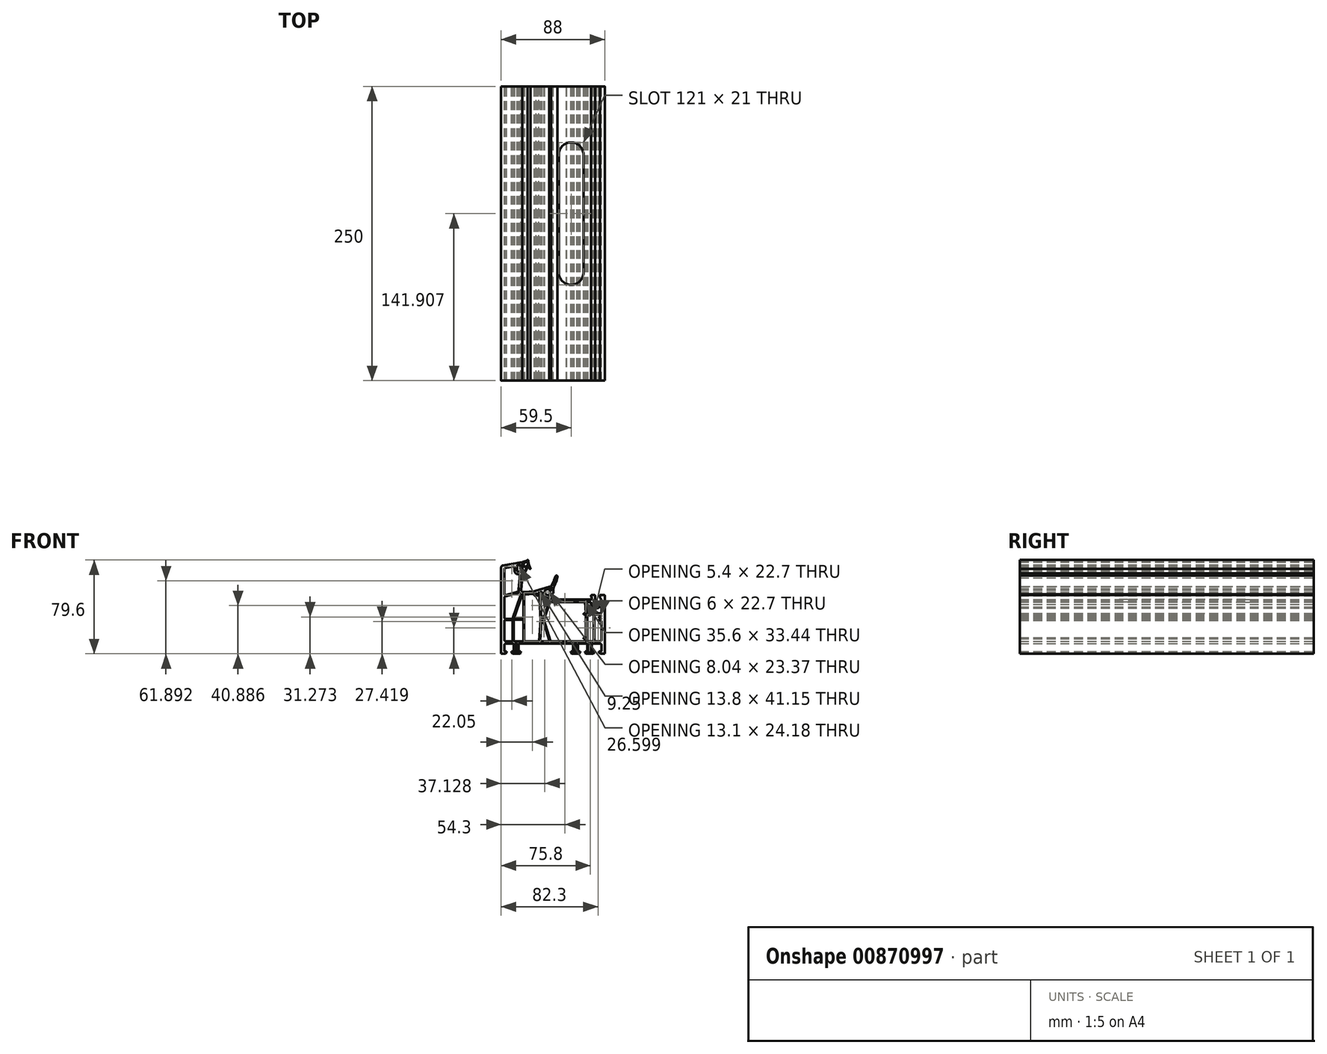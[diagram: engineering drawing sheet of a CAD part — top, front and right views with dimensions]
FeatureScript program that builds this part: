
annotation { "Feature Type Name" : "Feature", "Feature Type Description" : "" }
export const myFeature = defineFeature(function(context is Context, id is Id, definition is map)
    precondition{}
    {
        {
            var Q0;
            Q0=qCreatedBy(makeId("Front.planeOp"),FACE);
            var sketch = newSketch(context, id + "F0", { "sketchPlane" : qUnion([Q0])});
            skLineSegment(sketch, "E0", {"start": v(-41.3, 11) * mm, "end": v(-41.3, 32.34) * mm});
            skArc(sketch, "E1", {"start": v(-40.8, 32.84) * mm, "mid": v(-41.15, 32.7) * mm, "end": v(-41.3, 32.34) * mm});
            skLineSegment(sketch, "E2", {"start": v(-40.8, 32.84) * mm, "end": v(-33.29, 34.17) * mm});
            skArc(sketch, "E3", {"start": v(-32.7, 33.68) * mm, "mid": v(-32.88, 34.06) * mm, "end": v(-33.29, 34.17) * mm});
            skLineSegment(sketch, "E4", {"start": v(-32.7, 33.68) * mm, "end": v(-32.7, 30.97) * mm});
            skArc(sketch, "E5", {"start": v(-32.7, 30.97) * mm, "mid": v(-31.95, 28.92) * mm, "end": v(-30.06, 27.82) * mm});
            skLineSegment(sketch, "E6", {"start": v(-30.06, 27.82) * mm, "end": v(-28.61, 27.57) * mm});
            skArc(sketch, "E7", {"start": v(-28.2, 27.07) * mm, "mid": v(-28.32, 27.4) * mm, "end": v(-28.61, 27.57) * mm});
            skLineSegment(sketch, "E8", {"start": v(-28.2, 27.07) * mm, "end": v(-28.2, 24.7) * mm});
            skLineSegment(sketch, "E9", {"start": v(-28.2, 24.7) * mm, "end": v(-29.18, 14.92) * mm});
            skArc(sketch, "E10", {"start": v(-29.18, 14.92) * mm, "mid": v(-29.19, 14.2) * mm, "end": v(-29.08, 13.48) * mm});
            skArc(sketch, "E11", {"start": v(-29.43, 12.88) * mm, "mid": v(-29.13, 13.1) * mm, "end": v(-29.08, 13.48) * mm});
            skLineSegment(sketch, "E12", {"start": v(-29.43, 12.88) * mm, "end": v(-40.04, 10.04) * mm});
            skArc(sketch, "E13", {"start": v(-41.3, 11) * mm, "mid": v(-40.9, 10.2) * mm, "end": v(-40.04, 10.04) * mm});
            skLineSegment(sketch, "E14", {"start": v(-41.3, -9.1) * mm, "end": v(-41.3, 7.8) * mm});
            skArc(sketch, "E15", {"start": v(-40.56, 8.76) * mm, "mid": v(-41.1, 8.4) * mm, "end": v(-41.3, 7.8) * mm});
            skLineSegment(sketch, "E16", {"start": v(-40.56, 8.76) * mm, "end": v(-28.7, 11.94) * mm});
            skArc(sketch, "E17", {"start": v(-28.2, 11.78) * mm, "mid": v(-28.43, 11.93) * mm, "end": v(-28.7, 11.94) * mm});
            skArc(sketch, "E18", {"start": v(-28.2, 11.78) * mm, "mid": v(-27.87, 11.43) * mm, "end": v(-27.5, 11.13) * mm});
            skArc(sketch, "E19", {"start": v(-27.33, 10.56) * mm, "mid": v(-27.32, 10.87) * mm, "end": v(-27.5, 11.13) * mm});
            skLineSegment(sketch, "E20", {"start": v(-27.33, 10.56) * mm, "end": v(-34.25, -9.76) * mm});
            skArc(sketch, "E21", {"start": v(-34.72, -10.1) * mm, "mid": v(-34.43, -10) * mm, "end": v(-34.25, -9.76) * mm});
            skLineSegment(sketch, "E22", {"start": v(-34.72, -10.1) * mm, "end": v(-40.3, -10.1) * mm});
            skArc(sketch, "E23", {"start": v(-41.3, -9.1) * mm, "mid": v(-41, -9.8) * mm, "end": v(-40.3, -10.1) * mm});
            skLineSegment(sketch, "E24", {"start": v(-41.3, -28.1) * mm, "end": v(-41.3, -12.2) * mm});
            skArc(sketch, "E25", {"start": v(-40.3, -11.2) * mm, "mid": v(-41, -11.5) * mm, "end": v(-41.3, -12.2) * mm});
            skLineSegment(sketch, "E26", {"start": v(-40.3, -11.2) * mm, "end": v(-34.8, -11.2) * mm});
            skArc(sketch, "E27", {"start": v(-34.3, -11.7) * mm, "mid": v(-34.45, -11.35) * mm, "end": v(-34.8, -11.2) * mm});
            skLineSegment(sketch, "E28", {"start": v(-34.3, -11.7) * mm, "end": v(-34.3, -28.6) * mm});
            skArc(sketch, "E29", {"start": v(-34.8, -29.1) * mm, "mid": v(-34.45, -28.95) * mm, "end": v(-34.3, -28.6) * mm});
            skLineSegment(sketch, "E30", {"start": v(-34.8, -29.1) * mm, "end": v(-40.3, -29.1) * mm});
            skArc(sketch, "E31", {"start": v(-41.3, -28.1) * mm, "mid": v(-41, -28.8) * mm, "end": v(-40.3, -29.1) * mm});
            skLineSegment(sketch, "E32", {"start": v(-33.2, -28.6) * mm, "end": v(-33.2, -11.4) * mm});
            skArc(sketch, "E33", {"start": v(-32.7, -10.9) * mm, "mid": v(-33.05, -11.05) * mm, "end": v(-33.2, -11.4) * mm});
            skLineSegment(sketch, "E34", {"start": v(-32.7, -10.9) * mm, "end": v(-25.6, -10.9) * mm});
            skArc(sketch, "E35", {"start": v(-25.1, -11.4) * mm, "mid": v(-25.25, -11.05) * mm, "end": v(-25.6, -10.9) * mm});
            skLineSegment(sketch, "E36", {"start": v(-25.1, -11.4) * mm, "end": v(-25.1, -28.6) * mm});
            skArc(sketch, "E37", {"start": v(-25.6, -29.1) * mm, "mid": v(-25.25, -28.95) * mm, "end": v(-25.1, -28.6) * mm});
            skLineSegment(sketch, "E38", {"start": v(-25.6, -29.1) * mm, "end": v(-32.7, -29.1) * mm});
            skArc(sketch, "E39", {"start": v(-33.2, -28.6) * mm, "mid": v(-33.05, -28.95) * mm, "end": v(-32.7, -29.1) * mm});
            skLineSegment(sketch, "E40", {"start": v(-32.4, -31.8) * mm, "end": v(-32.4, -37.3) * mm});
            skArc(sketch, "E41", {"start": v(-32.84, -38.28) * mm, "mid": v(-32.52, -37.83) * mm, "end": v(-32.4, -37.3) * mm});
            skArc(sketch, "E42", {"start": v(-32.84, -38.27) * mm, "mid": v(-32.92, -38.6) * mm, "end": v(-32.64, -38.8) * mm});
            skLineSegment(sketch, "E43", {"start": v(-32.64, -38.8) * mm, "end": v(-29.76, -38.8) * mm});
            skArc(sketch, "E44", {"start": v(-29.76, -38.8) * mm, "mid": v(-29.48, -38.6) * mm, "end": v(-29.56, -38.27) * mm});
            skArc(sketch, "E45", {"start": v(-30, -37.3) * mm, "mid": v(-29.88, -37.83) * mm, "end": v(-29.56, -38.28) * mm});
            skLineSegment(sketch, "E46", {"start": v(-30, -37.3) * mm, "end": v(-30, -31.8) * mm});
            skArc(sketch, "E47", {"start": v(-30, -31.8) * mm, "mid": v(-30.15, -31.45) * mm, "end": v(-30.5, -31.3) * mm});
            skLineSegment(sketch, "E48", {"start": v(-30.5, -31.3) * mm, "end": v(-31.9, -31.3) * mm});
            skArc(sketch, "E49", {"start": v(-31.9, -31.3) * mm, "mid": v(-32.25, -31.45) * mm, "end": v(-32.4, -31.8) * mm});
            skLineSegment(sketch, "E50", {"start": v(-32.97, -9.44) * mm, "end": v(-26.34, 10.04) * mm});
            skArc(sketch, "E51", {"start": v(-25.78, 10.37) * mm, "mid": v(-26.12, 10.31) * mm, "end": v(-26.34, 10.04) * mm});
            skLineSegment(sketch, "E52", {"start": v(-25.78, 10.37) * mm, "end": v(-25.54, 10.33) * mm});
            skArc(sketch, "E53", {"start": v(-25.1, 9.84) * mm, "mid": v(-25.23, 10.17) * mm, "end": v(-25.54, 10.33) * mm});
            skLineSegment(sketch, "E54", {"start": v(-25.1, 9.84) * mm, "end": v(-25.1, -9.6) * mm});
            skArc(sketch, "E55", {"start": v(-25.6, -10.1) * mm, "mid": v(-25.25, -9.95) * mm, "end": v(-25.1, -9.6) * mm});
            skLineSegment(sketch, "E56", {"start": v(-25.6, -10.1) * mm, "end": v(-32.5, -10.1) * mm});
            skArc(sketch, "E57", {"start": v(-32.97, -9.44) * mm, "mid": v(-32.9, -9.9) * mm, "end": v(-32.5, -10.1) * mm});
            skLineSegment(sketch, "E58", {"start": v(-24.3, -28.6) * mm, "end": v(-24.3, 9.89) * mm});
            skArc(sketch, "E59", {"start": v(-23.84, 10.39) * mm, "mid": v(-24.17, 10.22) * mm, "end": v(-24.3, 9.89) * mm});
            skLineSegment(sketch, "E60", {"start": v(-23.84, 10.39) * mm, "end": v(-16.44, 11.03) * mm});
            skArc(sketch, "E61", {"start": v(-15.9, 10.53) * mm, "mid": v(-16.06, 10.9) * mm, "end": v(-16.44, 11.03) * mm});
            skLineSegment(sketch, "E62", {"start": v(-15.9, 10.53) * mm, "end": v(-15.9, 10.16) * mm});
            skArc(sketch, "E63", {"start": v(-15.9, 10.16) * mm, "mid": v(-15.3, 9.56) * mm, "end": v(-14.7, 10.16) * mm});
            skLineSegment(sketch, "E64", {"start": v(-14.7, 10.16) * mm, "end": v(-14.7, 10.9) * mm});
            skArc(sketch, "E65", {"start": v(-13.7, 10.9) * mm, "mid": v(-14.2, 11.4) * mm, "end": v(-14.7, 10.9) * mm});
            skLineSegment(sketch, "E66", {"start": v(-13.7, 10.9) * mm, "end": v(-13.7, 10.16) * mm});
            skArc(sketch, "E67", {"start": v(-13.7, 10.16) * mm, "mid": v(-13.1, 9.56) * mm, "end": v(-12.5, 10.16) * mm});
            skLineSegment(sketch, "E68", {"start": v(-12.5, 10.16) * mm, "end": v(-12.5, 11.63) * mm});
            skArc(sketch, "E69", {"start": v(-11.67, 11.65) * mm, "mid": v(-12.1, 12.05) * mm, "end": v(-12.5, 11.63) * mm});
            skLineSegment(sketch, "E70", {"start": v(-11.67, 11.65) * mm, "end": v(-10.5, -11.03) * mm});
            skLineSegment(sketch, "E71", {"start": v(-10.5, -11.03) * mm, "end": v(-11.67, -28.63) * mm});
            skArc(sketch, "E72", {"start": v(-12.17, -29.1) * mm, "mid": v(-11.83, -28.97) * mm, "end": v(-11.67, -28.63) * mm});
            skLineSegment(sketch, "E73", {"start": v(-12.17, -29.1) * mm, "end": v(-23.8, -29.1) * mm});
            skArc(sketch, "E74", {"start": v(-24.3, -28.6) * mm, "mid": v(-24.15, -28.95) * mm, "end": v(-23.8, -29.1) * mm});
            skLineSegment(sketch, "E75", {"start": v(-10.9, 12.03) * mm, "end": v(-9.74, -10.13) * mm});
            skArc(sketch, "E76", {"start": v(-9.74, -10.13) * mm, "mid": v(-9.59, -10.46) * mm, "end": v(-9.24, -10.6) * mm});
            skLineSegment(sketch, "E77", {"start": v(-9.24, -10.6) * mm, "end": v(-8.6, -10.6) * mm});
            skArc(sketch, "E78", {"start": v(-8.6, -10.6) * mm, "mid": v(-8.3, -10.5) * mm, "end": v(-8.12, -10.26) * mm});
            skLineSegment(sketch, "E79", {"start": v(-8.12, -10.26) * mm, "end": v(-2.88, 5.09) * mm});
            skArc(sketch, "E80", {"start": v(-2.88, 5.09) * mm, "mid": v(-2.85, 5.25) * mm, "end": v(-2.88, 5.41) * mm});
            skArc(sketch, "E81", {"start": v(-3.2, 6.76) * mm, "mid": v(-3.14, 6.13) * mm, "end": v(-2.94, 5.53) * mm});
            skArc(sketch, "E82", {"start": v(-3.2, 6.76) * mm, "mid": v(-3.28, 7.05) * mm, "end": v(-3.51, 7.24) * mm});
            skLineSegment(sketch, "E83", {"start": v(-3.51, 7.24) * mm, "end": v(-6.89, 8.6) * mm});
            skArc(sketch, "E84", {"start": v(-8.63, 10.05) * mm, "mid": v(-7.87, 9.2) * mm, "end": v(-6.89, 8.6) * mm});
            skArc(sketch, "E85", {"start": v(-9.2, 12.24) * mm, "mid": v(-9.08, 11.1) * mm, "end": v(-8.63, 10.05) * mm});
            skArc(sketch, "E86", {"start": v(-9.2, 12.24) * mm, "mid": v(-9.38, 12.67) * mm, "end": v(-9.84, 12.75) * mm});
            skLineSegment(sketch, "E87", {"start": v(-9.84, 12.75) * mm, "end": v(-10.54, 12.54) * mm});
            skArc(sketch, "E88", {"start": v(-10.54, 12.54) * mm, "mid": v(-10.8, 12.35) * mm, "end": v(-10.9, 12.03) * mm});
            skLineSegment(sketch, "E89", {"start": v(-10.86, -28.57) * mm, "end": v(-9.75, -11.87) * mm});
            skArc(sketch, "E90", {"start": v(-9.26, -11.4) * mm, "mid": v(-9.6, -11.53) * mm, "end": v(-9.75, -11.87) * mm});
            skLineSegment(sketch, "E91", {"start": v(-9.26, -11.4) * mm, "end": v(-8.61, -11.4) * mm});
            skArc(sketch, "E92", {"start": v(-8.13, -11.76) * mm, "mid": v(-8.31, -11.5) * mm, "end": v(-8.61, -11.4) * mm});
            skLineSegment(sketch, "E93", {"start": v(-8.13, -11.76) * mm, "end": v(-3.13, -28.46) * mm});
            skArc(sketch, "E94", {"start": v(-3.6, -29.1) * mm, "mid": v(-3.2, -28.9) * mm, "end": v(-3.13, -28.46) * mm});
            skLineSegment(sketch, "E95", {"start": v(-3.6, -29.1) * mm, "end": v(-10.36, -29.1) * mm});
            skArc(sketch, "E96", {"start": v(-10.86, -28.57) * mm, "mid": v(-10.73, -28.94) * mm, "end": v(-10.36, -29.1) * mm});
            skArc(sketch, "E97", {"start": v(-10.86, -28.57) * mm, "mid": v(-10.86, -28.57) * mm, "end": v(-10.86, -28.57) * mm});
            skLineSegment(sketch, "E98", {"start": v(-0.5, 4) * mm, "end": v(26.99, 4) * mm});
            skArc(sketch, "E99", {"start": v(27.28, 3.73) * mm, "mid": v(27.19, 3.92) * mm, "end": v(26.99, 4) * mm});
            skLineSegment(sketch, "E100", {"start": v(27.28, 3.73) * mm, "end": v(28.05, -5.06) * mm});
            skArc(sketch, "E101", {"start": v(27.55, -5.6) * mm, "mid": v(27.92, -5.44) * mm, "end": v(28.05, -5.06) * mm});
            skLineSegment(sketch, "E102", {"start": v(27.55, -5.6) * mm, "end": v(26.4, -5.6) * mm});
            skArc(sketch, "E103", {"start": v(26.4, -5.6) * mm, "mid": v(26.19, -5.69) * mm, "end": v(26.1, -5.9) * mm});
            skLineSegment(sketch, "E104", {"start": v(26.1, -5.9) * mm, "end": v(26.1, -6.1) * mm});
            skArc(sketch, "E105", {"start": v(26.1, -6.1) * mm, "mid": v(26.19, -6.31) * mm, "end": v(26.4, -6.4) * mm});
            skLineSegment(sketch, "E106", {"start": v(26.4, -6.4) * mm, "end": v(27.6, -6.4) * mm});
            skArc(sketch, "E107", {"start": v(28.1, -6.9) * mm, "mid": v(27.95, -6.55) * mm, "end": v(27.6, -6.4) * mm});
            skLineSegment(sketch, "E108", {"start": v(28.1, -6.9) * mm, "end": v(28.1, -25.7) * mm});
            skArc(sketch, "E109", {"start": v(27.6, -26.2) * mm, "mid": v(27.95, -26.05) * mm, "end": v(28.1, -25.7) * mm});
            skLineSegment(sketch, "E110", {"start": v(27.6, -26.2) * mm, "end": v(26.4, -26.2) * mm});
            skArc(sketch, "E111", {"start": v(26.4, -26.2) * mm, "mid": v(26.19, -26.29) * mm, "end": v(26.1, -26.5) * mm});
            skLineSegment(sketch, "E112", {"start": v(26.1, -26.5) * mm, "end": v(26.1, -26.7) * mm});
            skArc(sketch, "E113", {"start": v(26.1, -26.7) * mm, "mid": v(26.19, -26.91) * mm, "end": v(26.4, -27) * mm});
            skLineSegment(sketch, "E114", {"start": v(26.4, -27) * mm, "end": v(27.6, -27) * mm});
            skArc(sketch, "E115", {"start": v(28.1, -27.5) * mm, "mid": v(27.95, -27.15) * mm, "end": v(27.6, -27) * mm});
            skLineSegment(sketch, "E116", {"start": v(28.1, -27.5) * mm, "end": v(28.1, -28.8) * mm});
            skArc(sketch, "E117", {"start": v(27.8, -29.1) * mm, "mid": v(28.01, -29.01) * mm, "end": v(28.1, -28.8) * mm});
            skLineSegment(sketch, "E118", {"start": v(27.8, -29.1) * mm, "end": v(-1.73, -29.1) * mm});
            skArc(sketch, "E119", {"start": v(-2.2, -28.74) * mm, "mid": v(-2.03, -29) * mm, "end": v(-1.73, -29.1) * mm});
            skLineSegment(sketch, "E120", {"start": v(-2.2, -28.74) * mm, "end": v(-7.48, -11.15) * mm});
            skArc(sketch, "E121", {"start": v(-7.48, -10.87) * mm, "mid": v(-7.5, -11) * mm, "end": v(-7.48, -11.15) * mm});
            skLineSegment(sketch, "E122", {"start": v(-7.48, -10.87) * mm, "end": v(-2.4, 4) * mm});
            skArc(sketch, "E123", {"start": v(-1.7, 4.29) * mm, "mid": v(-2.12, 4.3) * mm, "end": v(-2.4, 4) * mm});
            skArc(sketch, "E124", {"start": v(-1.7, 4.29) * mm, "mid": v(-1.42, 4.16) * mm, "end": v(-1.12, 4.07) * mm});
            skArc(sketch, "E125", {"start": v(-1.12, 4.07) * mm, "mid": v(-0.81, 4.02) * mm, "end": v(-0.5, 4) * mm});
            skLineSegment(sketch, "E126", {"start": v(28.31, 3.46) * mm, "end": v(29.06, -5.14) * mm});
            skArc(sketch, "E127", {"start": v(29.06, -5.14) * mm, "mid": v(29.22, -5.47) * mm, "end": v(29.56, -5.6) * mm});
            skLineSegment(sketch, "E128", {"start": v(29.56, -5.6) * mm, "end": v(34, -5.6) * mm});
            skArc(sketch, "E129", {"start": v(34, -5.6) * mm, "mid": v(34.35, -5.45) * mm, "end": v(34.5, -5.1) * mm});
            skLineSegment(sketch, "E130", {"start": v(34.5, -5.1) * mm, "end": v(34.5, -0.18) * mm});
            skArc(sketch, "E131", {"start": v(34.5, -0.18) * mm, "mid": v(34.42, 0.1) * mm, "end": v(34.2, 0.27) * mm});
            skArc(sketch, "E132", {"start": v(32.3, 3.2) * mm, "mid": v(32.82, 1.46) * mm, "end": v(34.2, 0.27) * mm});
            skLineSegment(sketch, "E133", {"start": v(32.3, 3.2) * mm, "end": v(32.3, 3.5) * mm});
            skArc(sketch, "E134", {"start": v(32.3, 3.5) * mm, "mid": v(32.15, 3.85) * mm, "end": v(31.8, 4) * mm});
            skLineSegment(sketch, "E135", {"start": v(31.8, 4) * mm, "end": v(28.8, 4) * mm});
            skArc(sketch, "E136", {"start": v(28.8, 4) * mm, "mid": v(28.44, 3.84) * mm, "end": v(28.31, 3.46) * mm});
            skLineSegment(sketch, "E137", {"start": v(35.3, -5.1) * mm, "end": v(35.3, -0.5) * mm});
            skArc(sketch, "E138", {"start": v(35.8, 0) * mm, "mid": v(35.45, -0.15) * mm, "end": v(35.3, -0.5) * mm});
            skLineSegment(sketch, "E139", {"start": v(35.8, 0) * mm, "end": v(36.6, 0) * mm});
            skArc(sketch, "E140", {"start": v(37.1, -0.5) * mm, "mid": v(36.95, -0.15) * mm, "end": v(36.6, 0) * mm});
            skLineSegment(sketch, "E141", {"start": v(37.1, -0.5) * mm, "end": v(37.1, -0.6) * mm});
            skArc(sketch, "E142", {"start": v(37.1, -0.6) * mm, "mid": v(37.25, -0.95) * mm, "end": v(37.6, -1.1) * mm});
            skLineSegment(sketch, "E143", {"start": v(37.6, -1.1) * mm, "end": v(38.4, -1.1) * mm});
            skArc(sketch, "E144", {"start": v(38.4, -1.1) * mm, "mid": v(38.75, -0.95) * mm, "end": v(38.9, -0.6) * mm});
            skLineSegment(sketch, "E145", {"start": v(38.9, -0.6) * mm, "end": v(38.9, -0.5) * mm});
            skArc(sketch, "E146", {"start": v(39.4, 0) * mm, "mid": v(39.05, -0.15) * mm, "end": v(38.9, -0.5) * mm});
            skLineSegment(sketch, "E147", {"start": v(39.4, 0) * mm, "end": v(40.3, 0) * mm});
            skArc(sketch, "E148", {"start": v(41.3, -1) * mm, "mid": v(41, -0.3) * mm, "end": v(40.3, 0) * mm});
            skLineSegment(sketch, "E149", {"start": v(41.3, -1) * mm, "end": v(41.3, -4.6) * mm});
            skArc(sketch, "E150", {"start": v(40.3, -5.6) * mm, "mid": v(41, -5.3) * mm, "end": v(41.3, -4.6) * mm});
            skLineSegment(sketch, "E151", {"start": v(40.3, -5.6) * mm, "end": v(35.8, -5.6) * mm});
            skArc(sketch, "E152", {"start": v(35.3, -5.1) * mm, "mid": v(35.45, -5.45) * mm, "end": v(35.8, -5.6) * mm});
            skLineSegment(sketch, "E153", {"start": v(29.1, -6.9) * mm, "end": v(29.1, -28.6) * mm});
            skArc(sketch, "E154", {"start": v(29.1, -28.6) * mm, "mid": v(29.25, -28.95) * mm, "end": v(29.6, -29.1) * mm});
            skLineSegment(sketch, "E155", {"start": v(29.6, -29.1) * mm, "end": v(34, -29.1) * mm});
            skArc(sketch, "E156", {"start": v(34, -29.1) * mm, "mid": v(34.35, -28.95) * mm, "end": v(34.5, -28.6) * mm});
            skLineSegment(sketch, "E157", {"start": v(34.5, -28.6) * mm, "end": v(34.5, -6.9) * mm});
            skArc(sketch, "E158", {"start": v(34.5, -6.9) * mm, "mid": v(34.35, -6.55) * mm, "end": v(34, -6.4) * mm});
            skLineSegment(sketch, "E159", {"start": v(34, -6.4) * mm, "end": v(29.6, -6.4) * mm});
            skArc(sketch, "E160", {"start": v(29.6, -6.4) * mm, "mid": v(29.25, -6.55) * mm, "end": v(29.1, -6.9) * mm});
            skLineSegment(sketch, "E161", {"start": v(35.3, -6.9) * mm, "end": v(35.3, -28.6) * mm});
            skArc(sketch, "E162", {"start": v(35.3, -28.6) * mm, "mid": v(35.45, -28.95) * mm, "end": v(35.8, -29.1) * mm});
            skLineSegment(sketch, "E163", {"start": v(35.8, -29.1) * mm, "end": v(40.3, -29.1) * mm});
            skArc(sketch, "E164", {"start": v(40.3, -29.1) * mm, "mid": v(41, -28.8) * mm, "end": v(41.3, -28.1) * mm});
            skLineSegment(sketch, "E165", {"start": v(41.3, -28.1) * mm, "end": v(41.3, -12.6) * mm});
            skArc(sketch, "E166", {"start": v(41.3, -12.6) * mm, "mid": v(41, -11.9) * mm, "end": v(40.3, -11.6) * mm});
            skLineSegment(sketch, "E167", {"start": v(40.3, -11.6) * mm, "end": v(39.6, -11.6) * mm});
            skArc(sketch, "E168", {"start": v(39.6, -10.4) * mm, "mid": v(39, -11) * mm, "end": v(39.6, -11.6) * mm});
            skLineSegment(sketch, "E169", {"start": v(39.6, -10.4) * mm, "end": v(40.5, -10.4) * mm});
            skArc(sketch, "E170", {"start": v(40.5, -10.4) * mm, "mid": v(41, -9.9) * mm, "end": v(40.5, -9.4) * mm});
            skLineSegment(sketch, "E171", {"start": v(40.5, -9.4) * mm, "end": v(39.6, -9.4) * mm});
            skArc(sketch, "E172", {"start": v(39.6, -8.2) * mm, "mid": v(39, -8.8) * mm, "end": v(39.6, -9.4) * mm});
            skLineSegment(sketch, "E173", {"start": v(39.6, -8.2) * mm, "end": v(40.5, -8.2) * mm});
            skArc(sketch, "E174", {"start": v(40.5, -8.2) * mm, "mid": v(41, -7.7) * mm, "end": v(40.5, -7.2) * mm});
            skLineSegment(sketch, "E175", {"start": v(40.5, -7.2) * mm, "end": v(39.6, -7.2) * mm});
            skArc(sketch, "E176", {"start": v(39.02, -6.76) * mm, "mid": v(39.24, -7.08) * mm, "end": v(39.6, -7.2) * mm});
            skArc(sketch, "E177", {"start": v(39.02, -6.76) * mm, "mid": v(38.84, -6.5) * mm, "end": v(38.54, -6.4) * mm});
            skLineSegment(sketch, "E178", {"start": v(38.54, -6.4) * mm, "end": v(35.8, -6.4) * mm});
            skArc(sketch, "E179", {"start": v(35.8, -6.4) * mm, "mid": v(35.45, -6.55) * mm, "end": v(35.3, -6.9) * mm});
            skLineSegment(sketch, "E180", {"start": v(30, -31.8) * mm, "end": v(30, -37.3) * mm});
            skArc(sketch, "E181", {"start": v(29.56, -38.28) * mm, "mid": v(29.88, -37.83) * mm, "end": v(30, -37.3) * mm});
            skArc(sketch, "E182", {"start": v(29.56, -38.27) * mm, "mid": v(29.48, -38.6) * mm, "end": v(29.76, -38.8) * mm});
            skLineSegment(sketch, "E183", {"start": v(29.76, -38.8) * mm, "end": v(32.64, -38.8) * mm});
            skArc(sketch, "E184", {"start": v(32.64, -38.8) * mm, "mid": v(32.92, -38.6) * mm, "end": v(32.84, -38.27) * mm});
            skArc(sketch, "E185", {"start": v(32.4, -37.3) * mm, "mid": v(32.52, -37.83) * mm, "end": v(32.84, -38.28) * mm});
            skLineSegment(sketch, "E186", {"start": v(32.4, -37.3) * mm, "end": v(32.4, -31.8) * mm});
            skArc(sketch, "E187", {"start": v(32.4, -31.8) * mm, "mid": v(32.25, -31.45) * mm, "end": v(31.9, -31.3) * mm});
            skLineSegment(sketch, "E188", {"start": v(31.9, -31.3) * mm, "end": v(30.5, -31.3) * mm});
            skArc(sketch, "E189", {"start": v(30.5, -31.3) * mm, "mid": v(30.15, -31.45) * mm, "end": v(30, -31.8) * mm});
            skLineSegment(sketch, "E190", {"start": v(18, -37.3) * mm, "end": v(18, -31.8) * mm});
            skArc(sketch, "E191", {"start": v(18.5, -31.3) * mm, "mid": v(18.15, -31.45) * mm, "end": v(18, -31.8) * mm});
            skLineSegment(sketch, "E192", {"start": v(18.5, -31.3) * mm, "end": v(19.9, -31.3) * mm});
            skArc(sketch, "E193", {"start": v(20.4, -31.8) * mm, "mid": v(20.25, -31.45) * mm, "end": v(19.9, -31.3) * mm});
            skLineSegment(sketch, "E194", {"start": v(20.4, -31.8) * mm, "end": v(20.4, -37.3) * mm});
            skArc(sketch, "E195", {"start": v(20.4, -37.3) * mm, "mid": v(20.52, -37.83) * mm, "end": v(20.84, -38.27) * mm});
            skArc(sketch, "E196", {"start": v(20.64, -38.8) * mm, "mid": v(20.92, -38.6) * mm, "end": v(20.84, -38.27) * mm});
            skLineSegment(sketch, "E197", {"start": v(20.64, -38.8) * mm, "end": v(17.76, -38.8) * mm});
            skArc(sketch, "E198", {"start": v(17.56, -38.28) * mm, "mid": v(17.48, -38.6) * mm, "end": v(17.76, -38.8) * mm});
            skArc(sketch, "E199", {"start": v(17.56, -38.28) * mm, "mid": v(17.88, -37.83) * mm, "end": v(18, -37.3) * mm});
            skLineSegment(sketch, "E200", {"start": v(30.5, -31.3) * mm, "end": v(31.9, -31.3) * mm});
            skLineSegment(sketch, "E201", {"start": v(32.4, -31.8) * mm, "end": v(32.4, -37.3) * mm});
            skLineSegment(sketch, "E202", {"start": v(32.64, -38.8) * mm, "end": v(29.76, -38.8) * mm});
            skLineSegment(sketch, "E203", {"start": v(30, -37.3) * mm, "end": v(30, -31.8) * mm});
            skArc(sketch, "E204", {"start": v(17.56, -38.28) * mm, "mid": v(17.89, -37.83) * mm, "end": v(18, -37.3) * mm});
            skLineSegment(sketch, "E205", {"start": v(35.8, -6.4) * mm, "end": v(38.54, -6.4) * mm});
            skLineSegment(sketch, "E206", {"start": v(39.6, -7.2) * mm, "end": v(40.5, -7.2) * mm});
            skLineSegment(sketch, "E207", {"start": v(40.5, -8.2) * mm, "end": v(39.6, -8.2) * mm});
            skLineSegment(sketch, "E208", {"start": v(39.6, -9.4) * mm, "end": v(40.5, -9.4) * mm});
            skLineSegment(sketch, "E209", {"start": v(40.5, -10.4) * mm, "end": v(39.6, -10.4) * mm});
            skLineSegment(sketch, "E210", {"start": v(39.6, -11.6) * mm, "end": v(40.3, -11.6) * mm});
            skLineSegment(sketch, "E211", {"start": v(41.3, -12.6) * mm, "end": v(41.3, -28.1) * mm});
            skLineSegment(sketch, "E212", {"start": v(40.3, -29.1) * mm, "end": v(35.8, -29.1) * mm});
            skLineSegment(sketch, "E213", {"start": v(35.3, -28.6) * mm, "end": v(35.3, -6.9) * mm});
            skArc(sketch, "E214", {"start": v(38.4, -1.1) * mm, "mid": v(38.77, -0.94) * mm, "end": v(38.9, -0.55) * mm});
            skArc(sketch, "E215", {"start": v(39.4, 0) * mm, "mid": v(39.03, -0.16) * mm, "end": v(38.9, -0.55) * mm});
            skLineSegment(sketch, "E216", {"start": v(29.6, -6.4) * mm, "end": v(34, -6.4) * mm});
            skLineSegment(sketch, "E217", {"start": v(34.5, -6.9) * mm, "end": v(34.5, -28.6) * mm});
            skLineSegment(sketch, "E218", {"start": v(34, -29.1) * mm, "end": v(29.6, -29.1) * mm});
            skLineSegment(sketch, "E219", {"start": v(29.1, -28.6) * mm, "end": v(29.1, -6.9) * mm});
            skLineSegment(sketch, "E220", {"start": v(28.8, 4) * mm, "end": v(31.8, 4) * mm});
            skLineSegment(sketch, "E221", {"start": v(32.3, 3.5) * mm, "end": v(32.3, 3.2) * mm});
            skLineSegment(sketch, "E222", {"start": v(34.5, -0.18) * mm, "end": v(34.5, -5.1) * mm});
            skLineSegment(sketch, "E223", {"start": v(34, -5.6) * mm, "end": v(29.56, -5.6) * mm});
            skLineSegment(sketch, "E224", {"start": v(29.06, -5.14) * mm, "end": v(28.31, 3.46) * mm});
            skLineSegment(sketch, "E225", {"start": v(-31.9, -31.3) * mm, "end": v(-30.5, -31.3) * mm});
            skLineSegment(sketch, "E226", {"start": v(-30, -31.8) * mm, "end": v(-30, -37.3) * mm});
            skLineSegment(sketch, "E227", {"start": v(-29.76, -38.8) * mm, "end": v(-32.64, -38.8) * mm});
            skLineSegment(sketch, "E228", {"start": v(-32.4, -37.3) * mm, "end": v(-32.4, -31.8) * mm});
            skLineSegment(sketch, "E229", {"start": v(-1.73, -29.1) * mm, "end": v(27.8, -29.1) * mm});
            skLineSegment(sketch, "E230", {"start": v(28.1, -28.8) * mm, "end": v(28.1, -27.5) * mm});
            skLineSegment(sketch, "E231", {"start": v(27.6, -27) * mm, "end": v(26.4, -27) * mm});
            skLineSegment(sketch, "E232", {"start": v(26.1, -26.7) * mm, "end": v(26.1, -26.5) * mm});
            skLineSegment(sketch, "E233", {"start": v(26.4, -26.2) * mm, "end": v(27.6, -26.2) * mm});
            skLineSegment(sketch, "E234", {"start": v(28.1, -25.7) * mm, "end": v(28.1, -6.9) * mm});
            skLineSegment(sketch, "E235", {"start": v(27.6, -6.4) * mm, "end": v(26.4, -6.4) * mm});
            skLineSegment(sketch, "E236", {"start": v(26.1, -6.1) * mm, "end": v(26.1, -5.9) * mm});
            skLineSegment(sketch, "E237", {"start": v(26.4, -5.6) * mm, "end": v(27.55, -5.6) * mm});
            skLineSegment(sketch, "E238", {"start": v(28.05, -5.06) * mm, "end": v(27.28, 3.73) * mm});
            skLineSegment(sketch, "E239", {"start": v(26.99, 4) * mm, "end": v(-0.5, 4) * mm});
            skLineSegment(sketch, "E240", {"start": v(-2.4, 4) * mm, "end": v(-7.48, -10.87) * mm});
            skLineSegment(sketch, "E241", {"start": v(-7.48, -11.15) * mm, "end": v(-2.2, -28.74) * mm});
            skLineSegment(sketch, "E242", {"start": v(-10.54, 12.54) * mm, "end": v(-9.84, 12.75) * mm});
            skLineSegment(sketch, "E243", {"start": v(-6.89, 8.6) * mm, "end": v(-3.51, 7.24) * mm});
            skArc(sketch, "E244", {"start": v(-2.88, 5.09) * mm, "mid": v(-2.86, 5.32) * mm, "end": v(-2.94, 5.53) * mm});
            skLineSegment(sketch, "E245", {"start": v(-2.88, 5.09) * mm, "end": v(-8.12, -10.26) * mm});
            skLineSegment(sketch, "E246", {"start": v(-8.6, -10.6) * mm, "end": v(-9.24, -10.6) * mm});
            skLineSegment(sketch, "E247", {"start": v(-9.74, -10.13) * mm, "end": v(-10.9, 12.03) * mm});
            skLineSegment(sketch, "E248", {"start": v(-32.5, -10.1) * mm, "end": v(-25.6, -10.1) * mm});
            skLineSegment(sketch, "E249", {"start": v(-25.1, -9.6) * mm, "end": v(-25.1, 9.84) * mm});
            skLineSegment(sketch, "E250", {"start": v(-26.34, 10.04) * mm, "end": v(-32.97, -9.44) * mm});
            skLineSegment(sketch, "E251", {"start": v(-41.3, 7.8) * mm, "end": v(-41.3, -9.1) * mm});
            skLineSegment(sketch, "E252", {"start": v(-40.3, -10.1) * mm, "end": v(-34.72, -10.1) * mm});
            skLineSegment(sketch, "E253", {"start": v(-34.25, -9.76) * mm, "end": v(-27.33, 10.57) * mm});
            skArc(sketch, "E254", {"start": v(-27.33, 10.57) * mm, "mid": v(-27.32, 10.88) * mm, "end": v(-27.5, 11.13) * mm});
            skArc(sketch, "E255", {"start": v(-28.2, 11.77) * mm, "mid": v(-27.87, 11.43) * mm, "end": v(-27.5, 11.13) * mm});
            skArc(sketch, "E256", {"start": v(-28.2, 11.77) * mm, "mid": v(-28.43, 11.93) * mm, "end": v(-28.71, 11.93) * mm});
            skLineSegment(sketch, "E257", {"start": v(-28.71, 11.93) * mm, "end": v(-40.56, 8.76) * mm});
            skLineSegment(sketch, "E258", {"start": v(-29.18, 14.92) * mm, "end": v(-28.2, 24.7) * mm});
            skLineSegment(sketch, "E259", {"start": v(-28.2, 24.7) * mm, "end": v(-28.2, 27.07) * mm});
            skLineSegment(sketch, "E260", {"start": v(-28.61, 27.57) * mm, "end": v(-30.06, 27.82) * mm});
            skLineSegment(sketch, "E261", {"start": v(-32.7, 30.97) * mm, "end": v(-32.7, 33.68) * mm});
            skLineSegment(sketch, "E262", {"start": v(-33.29, 34.17) * mm, "end": v(-40.8, 32.84) * mm});
            skLineSegment(sketch, "E263", {"start": v(-41.3, 32.34) * mm, "end": v(-41.3, 11) * mm});
            skLineSegment(sketch, "E264", {"start": v(-40.04, 10.04) * mm, "end": v(-29.43, 12.88) * mm});
            skArc(sketch, "E265", {"start": v(-29.67, 35.52) * mm, "mid": v(-30.27, 35.18) * mm, "end": v(-30.5, 34.54) * mm});
            skLineSegment(sketch, "E266", {"start": v(-29.67, 35.52) * mm, "end": v(-28.09, 35.8) * mm});
            skArc(sketch, "E267", {"start": v(-27.5, 35.3) * mm, "mid": v(-27.68, 35.7) * mm, "end": v(-28.09, 35.8) * mm});
            skLineSegment(sketch, "E268", {"start": v(-27.5, 35.3) * mm, "end": v(-27.5, 34.2) * mm});
            skLineSegment(sketch, "E269", {"start": v(-27.5, 34.2) * mm, "end": v(-26.7, 34.2) * mm});
            skArc(sketch, "E270", {"start": v(-26.7, 34.2) * mm, "mid": v(-26.2, 34.4) * mm, "end": v(-26, 34.9) * mm});
            skLineSegment(sketch, "E271", {"start": v(-26, 34.9) * mm, "end": v(-26, 38.2) * mm});
            skLineSegment(sketch, "E272", {"start": v(-26, 38.2) * mm, "end": v(-42.35, 35.32) * mm});
            skArc(sketch, "E273", {"start": v(-42.35, 35.32) * mm, "mid": v(-43.53, 34.63) * mm, "end": v(-44, 33.35) * mm});
            skLineSegment(sketch, "E274", {"start": v(-44, 33.35) * mm, "end": v(-44, -39.8) * mm});
            skLineSegment(sketch, "E275", {"start": v(-44, -39.8) * mm, "end": v(-40.2, -39.8) * mm});
            skLineSegment(sketch, "E276", {"start": v(-40.2, -39.8) * mm, "end": v(-39.2, -38.8) * mm});
            skLineSegment(sketch, "E277", {"start": v(-39.2, -38.8) * mm, "end": v(-39.2, -37.8) * mm});
            skLineSegment(sketch, "E278", {"start": v(-39.2, -37.8) * mm, "end": v(-40.8, -37.8) * mm});
            skArc(sketch, "E279", {"start": v(-41.3, -37.3) * mm, "mid": v(-41.15, -37.65) * mm, "end": v(-40.8, -37.8) * mm});
            skLineSegment(sketch, "E280", {"start": v(-41.3, -37.3) * mm, "end": v(-41.3, -32.3) * mm});
            skArc(sketch, "E281", {"start": v(-40.3, -31.3) * mm, "mid": v(-41, -31.6) * mm, "end": v(-41.3, -32.3) * mm});
            skLineSegment(sketch, "E282", {"start": v(-40.3, -31.3) * mm, "end": v(-33.7, -31.3) * mm});
            skArc(sketch, "E283", {"start": v(-33.2, -31.8) * mm, "mid": v(-33.35, -31.45) * mm, "end": v(-33.7, -31.3) * mm});
            skLineSegment(sketch, "E284", {"start": v(-33.2, -31.8) * mm, "end": v(-33.2, -37.3) * mm});
            skArc(sketch, "E285", {"start": v(-33.7, -37.8) * mm, "mid": v(-33.35, -37.65) * mm, "end": v(-33.2, -37.3) * mm});
            skLineSegment(sketch, "E286", {"start": v(-33.7, -37.8) * mm, "end": v(-35.2, -37.8) * mm});
            skLineSegment(sketch, "E287", {"start": v(-35.2, -37.8) * mm, "end": v(-35.2, -38.8) * mm});
            skLineSegment(sketch, "E288", {"start": v(-35.2, -38.8) * mm, "end": v(-34.4, -39.6) * mm});
            skLineSegment(sketch, "E289", {"start": v(-34.4, -39.6) * mm, "end": v(-28, -39.6) * mm});
            skLineSegment(sketch, "E290", {"start": v(-28, -39.6) * mm, "end": v(-27.2, -38.8) * mm});
            skLineSegment(sketch, "E291", {"start": v(-27.2, -38.8) * mm, "end": v(-27.2, -37.8) * mm});
            skLineSegment(sketch, "E292", {"start": v(-27.2, -37.8) * mm, "end": v(-28.7, -37.8) * mm});
            skArc(sketch, "E293", {"start": v(-29.2, -37.3) * mm, "mid": v(-29.05, -37.65) * mm, "end": v(-28.7, -37.8) * mm});
            skLineSegment(sketch, "E294", {"start": v(-29.2, -37.3) * mm, "end": v(-29.2, -31.8) * mm});
            skArc(sketch, "E295", {"start": v(-28.7, -31.3) * mm, "mid": v(-29.05, -31.45) * mm, "end": v(-29.2, -31.8) * mm});
            skLineSegment(sketch, "E296", {"start": v(-28.7, -31.3) * mm, "end": v(11.38, -31.3) * mm});
            skLineSegment(sketch, "E297", {"start": v(11.38, -31.3) * mm, "end": v(11.5, -31.1) * mm});
            skLineSegment(sketch, "E298", {"start": v(11.5, -31.1) * mm, "end": v(11.62, -31.3) * mm});
            skLineSegment(sketch, "E299", {"start": v(11.62, -31.3) * mm, "end": v(16.7, -31.3) * mm});
            skArc(sketch, "E300", {"start": v(17.2, -31.8) * mm, "mid": v(17.05, -31.45) * mm, "end": v(16.7, -31.3) * mm});
            skLineSegment(sketch, "E301", {"start": v(17.2, -31.8) * mm, "end": v(17.2, -37.3) * mm});
            skArc(sketch, "E302", {"start": v(16.7, -37.8) * mm, "mid": v(17.05, -37.65) * mm, "end": v(17.2, -37.3) * mm});
            skLineSegment(sketch, "E303", {"start": v(16.7, -37.8) * mm, "end": v(15.2, -37.8) * mm});
            skLineSegment(sketch, "E304", {"start": v(15.2, -37.8) * mm, "end": v(15.2, -38.8) * mm});
            skLineSegment(sketch, "E305", {"start": v(15.2, -38.8) * mm, "end": v(16, -39.6) * mm});
            skLineSegment(sketch, "E306", {"start": v(16, -39.6) * mm, "end": v(22.4, -39.6) * mm});
            skLineSegment(sketch, "E307", {"start": v(22.4, -39.6) * mm, "end": v(23.2, -38.8) * mm});
            skLineSegment(sketch, "E308", {"start": v(23.2, -38.8) * mm, "end": v(23.2, -37.8) * mm});
            skLineSegment(sketch, "E309", {"start": v(23.2, -37.8) * mm, "end": v(21.7, -37.8) * mm});
            skArc(sketch, "E310", {"start": v(21.2, -37.3) * mm, "mid": v(21.35, -37.65) * mm, "end": v(21.7, -37.8) * mm});
            skLineSegment(sketch, "E311", {"start": v(21.2, -37.3) * mm, "end": v(21.2, -31.8) * mm});
            skArc(sketch, "E312", {"start": v(21.7, -31.3) * mm, "mid": v(21.35, -31.45) * mm, "end": v(21.2, -31.8) * mm});
            skLineSegment(sketch, "E313", {"start": v(21.7, -31.3) * mm, "end": v(28.7, -31.3) * mm});
            skArc(sketch, "E314", {"start": v(29.2, -31.8) * mm, "mid": v(29.05, -31.45) * mm, "end": v(28.7, -31.3) * mm});
            skLineSegment(sketch, "E315", {"start": v(29.2, -31.8) * mm, "end": v(29.2, -37.3) * mm});
            skArc(sketch, "E316", {"start": v(28.7, -37.8) * mm, "mid": v(29.05, -37.65) * mm, "end": v(29.2, -37.3) * mm});
            skLineSegment(sketch, "E317", {"start": v(28.7, -37.8) * mm, "end": v(27.2, -37.8) * mm});
            skLineSegment(sketch, "E318", {"start": v(27.2, -37.8) * mm, "end": v(27.2, -38.8) * mm});
            skLineSegment(sketch, "E319", {"start": v(27.2, -38.8) * mm, "end": v(28, -39.6) * mm});
            skLineSegment(sketch, "E320", {"start": v(28, -39.6) * mm, "end": v(34.4, -39.6) * mm});
            skLineSegment(sketch, "E321", {"start": v(34.4, -39.6) * mm, "end": v(35.2, -38.8) * mm});
            skLineSegment(sketch, "E322", {"start": v(35.2, -38.8) * mm, "end": v(35.2, -37.8) * mm});
            skLineSegment(sketch, "E323", {"start": v(35.2, -37.8) * mm, "end": v(33.7, -37.8) * mm});
            skArc(sketch, "E324", {"start": v(33.2, -37.3) * mm, "mid": v(33.35, -37.65) * mm, "end": v(33.7, -37.8) * mm});
            skLineSegment(sketch, "E325", {"start": v(33.2, -37.3) * mm, "end": v(33.2, -31.8) * mm});
            skArc(sketch, "E326", {"start": v(33.7, -31.3) * mm, "mid": v(33.35, -31.45) * mm, "end": v(33.2, -31.8) * mm});
            skLineSegment(sketch, "E327", {"start": v(33.7, -31.3) * mm, "end": v(40.3, -31.3) * mm});
            skArc(sketch, "E328", {"start": v(41.3, -32.3) * mm, "mid": v(41, -31.6) * mm, "end": v(40.3, -31.3) * mm});
            skLineSegment(sketch, "E329", {"start": v(41.3, -32.3) * mm, "end": v(41.3, -37.3) * mm});
            skArc(sketch, "E330", {"start": v(40.8, -37.8) * mm, "mid": v(41.15, -37.65) * mm, "end": v(41.3, -37.3) * mm});
            skLineSegment(sketch, "E331", {"start": v(40.8, -37.8) * mm, "end": v(39.2, -37.8) * mm});
            skLineSegment(sketch, "E332", {"start": v(39.2, -37.8) * mm, "end": v(39.2, -38.8) * mm});
            skLineSegment(sketch, "E333", {"start": v(39.2, -38.8) * mm, "end": v(40.2, -39.8) * mm});
            skLineSegment(sketch, "E334", {"start": v(40.2, -39.8) * mm, "end": v(44, -39.8) * mm});
            skLineSegment(sketch, "E335", {"start": v(44, -39.8) * mm, "end": v(44, 9.7) * mm});
            skArc(sketch, "E336", {"start": v(44, 9.7) * mm, "mid": v(43.85, 10.05) * mm, "end": v(43.5, 10.2) * mm});
            skLineSegment(sketch, "E337", {"start": v(43.5, 10.2) * mm, "end": v(40.5, 10.2) * mm});
            skArc(sketch, "E338", {"start": v(40.5, 10.2) * mm, "mid": v(40.15, 10.05) * mm, "end": v(40, 9.7) * mm});
            skLineSegment(sketch, "E339", {"start": v(40, 9.7) * mm, "end": v(40, 8.2) * mm});
            skArc(sketch, "E340", {"start": v(40, 8.2) * mm, "mid": v(40.09, 7.8) * mm, "end": v(40.33, 7.45) * mm});
            skArc(sketch, "E341", {"start": v(41, 5.96) * mm, "mid": v(40.83, 6.78) * mm, "end": v(40.33, 7.45) * mm});
            skLineSegment(sketch, "E342", {"start": v(41, 5.96) * mm, "end": v(41, 4.2) * mm});
            skArc(sketch, "E343", {"start": v(39, 2.2) * mm, "mid": v(40.41, 2.79) * mm, "end": v(41, 4.2) * mm});
            skLineSegment(sketch, "E344", {"start": v(39, 2.2) * mm, "end": v(35.5, 2.2) * mm});
            skArc(sketch, "E345", {"start": v(34.5, 3.2) * mm, "mid": v(34.8, 2.5) * mm, "end": v(35.5, 2.2) * mm});
            skLineSegment(sketch, "E346", {"start": v(34.5, 3.2) * mm, "end": v(34.5, 3.7) * mm});
            skArc(sketch, "E347", {"start": v(35.5, 4.7) * mm, "mid": v(34.8, 4.4) * mm, "end": v(34.5, 3.7) * mm});
            skLineSegment(sketch, "E348", {"start": v(35.5, 4.7) * mm, "end": v(36, 4.7) * mm});
            skLineSegment(sketch, "E349", {"start": v(36, 4.7) * mm, "end": v(36, 9.5) * mm});
            skArc(sketch, "E350", {"start": v(36, 9.5) * mm, "mid": v(35.85, 9.85) * mm, "end": v(35.5, 10) * mm});
            skLineSegment(sketch, "E351", {"start": v(35.5, 10) * mm, "end": v(33, 10) * mm});
            skArc(sketch, "E352", {"start": v(33, 10) * mm, "mid": v(32.6, 9.8) * mm, "end": v(32.52, 9.35) * mm});
            skLineSegment(sketch, "E353", {"start": v(32.52, 9.35) * mm, "end": v(33.12, 7.51) * mm});
            skArc(sketch, "E354", {"start": v(32.17, 6.2) * mm, "mid": v(32.98, 6.61) * mm, "end": v(33.12, 7.51) * mm});
            skLineSegment(sketch, "E355", {"start": v(32.17, 6.2) * mm, "end": v(-0.5, 6.2) * mm});
            skArc(sketch, "E356", {"start": v(-1, 6.7) * mm, "mid": v(-0.85, 6.35) * mm, "end": v(-0.5, 6.2) * mm});
            skLineSegment(sketch, "E357", {"start": v(-1, 6.7) * mm, "end": v(-1, 10.3) * mm});
            skArc(sketch, "E358", {"start": v(-1, 10.3) * mm, "mid": v(-1.2, 10.8) * mm, "end": v(-1.7, 11) * mm});
            skLineSegment(sketch, "E359", {"start": v(-1.7, 11) * mm, "end": v(-2.5, 11) * mm});
            skLineSegment(sketch, "E360", {"start": v(-2.5, 11) * mm, "end": v(-2.5, 9.94) * mm});
            skArc(sketch, "E361", {"start": v(-3.19, 9.48) * mm, "mid": v(-2.72, 9.53) * mm, "end": v(-2.5, 9.94) * mm});
            skLineSegment(sketch, "E362", {"start": v(-3.19, 9.48) * mm, "end": v(-6.06, 10.64) * mm});
            skArc(sketch, "E363", {"start": v(-7, 12.03) * mm, "mid": v(-6.74, 11.2) * mm, "end": v(-6.06, 10.64) * mm});
            skLineSegment(sketch, "E364", {"start": v(-7, 12.03) * mm, "end": v(-7, 13.24) * mm});
            skArc(sketch, "E365", {"start": v(-5.94, 14.67) * mm, "mid": v(-6.7, 14.13) * mm, "end": v(-7, 13.24) * mm});
            skLineSegment(sketch, "E366", {"start": v(-5.94, 14.67) * mm, "end": v(-3.15, 15.53) * mm});
            skArc(sketch, "E367", {"start": v(-2.5, 15.05) * mm, "mid": v(-2.7, 15.45) * mm, "end": v(-3.15, 15.53) * mm});
            skLineSegment(sketch, "E368", {"start": v(-2.5, 15.05) * mm, "end": v(-2.5, 14.2) * mm});
            skLineSegment(sketch, "E369", {"start": v(-2.5, 14.2) * mm, "end": v(-1.7, 14.2) * mm});
            skArc(sketch, "E370", {"start": v(-1.7, 14.2) * mm, "mid": v(-1.2, 14.4) * mm, "end": v(-1, 14.9) * mm});
            skLineSegment(sketch, "E371", {"start": v(-1, 14.9) * mm, "end": v(-1, 17.2) * mm});
            skLineSegment(sketch, "E372", {"start": v(-1, 17.2) * mm, "end": v(-2.58, 17.2) * mm});
            skArc(sketch, "E373", {"start": v(-3.01, 17.13) * mm, "mid": v(-2.8, 17.15) * mm, "end": v(-2.58, 17.2) * mm});
            skLineSegment(sketch, "E374", {"start": v(-3.01, 17.13) * mm, "end": v(-15, 13.48) * mm});
            skArc(sketch, "E375", {"start": v(-16.02, 13.28) * mm, "mid": v(-15.5, 13.35) * mm, "end": v(-15, 13.48) * mm});
            skLineSegment(sketch, "E376", {"start": v(-16.02, 13.28) * mm, "end": v(-24.83, 12.5) * mm});
            skArc(sketch, "E377", {"start": v(-27, 14.7) * mm, "mid": v(-26.42, 13.1) * mm, "end": v(-24.83, 12.5) * mm});
            skLineSegment(sketch, "E378", {"start": v(-27, 14.7) * mm, "end": v(-26, 24.6) * mm});
            skLineSegment(sketch, "E379", {"start": v(-26, 24.6) * mm, "end": v(-26, 30.3) * mm});
            skArc(sketch, "E380", {"start": v(-26, 30.3) * mm, "mid": v(-26.2, 30.8) * mm, "end": v(-26.7, 31) * mm});
            skLineSegment(sketch, "E381", {"start": v(-26.7, 31) * mm, "end": v(-27.5, 31) * mm});
            skLineSegment(sketch, "E382", {"start": v(-27.5, 31) * mm, "end": v(-27.5, 30.2) * mm});
            skArc(sketch, "E383", {"start": v(-28.09, 29.7) * mm, "mid": v(-27.68, 29.82) * mm, "end": v(-27.5, 30.2) * mm});
            skLineSegment(sketch, "E384", {"start": v(-28.09, 29.7) * mm, "end": v(-29.67, 29.99) * mm});
            skArc(sketch, "E385", {"start": v(-30.5, 30.97) * mm, "mid": v(-30.27, 30.33) * mm, "end": v(-29.67, 29.99) * mm});
            skLineSegment(sketch, "E386", {"start": v(-30.5, 30.97) * mm, "end": v(-30.5, 34.54) * mm});
            skLineSegment(sketch, "E387", {"start": v(-1.5, 17.2) * mm, "end": v(-1, 17.2) * mm});
            skLineSegment(sketch, "E388", {"start": v(-1, 17.2) * mm, "end": v(-1, 14.9) * mm});
            skLineSegment(sketch, "E389", {"start": v(-1.7, 14.2) * mm, "end": v(-2.5, 14.2) * mm});
            skLineSegment(sketch, "E390", {"start": v(-2.5, 14.2) * mm, "end": v(-2.5, 14.45) * mm});
            skLineSegment(sketch, "E391", {"start": v(-2.5, 10.75) * mm, "end": v(-2.5, 11) * mm});
            skLineSegment(sketch, "E392", {"start": v(-2.5, 11) * mm, "end": v(-1.7, 11) * mm});
            skArc(sketch, "E393", {"start": v(-1.23, 10.82) * mm, "mid": v(-1.45, 10.95) * mm, "end": v(-1.7, 11) * mm});
            skLineSegment(sketch, "E394", {"start": v(-26.7, 34.2) * mm, "end": v(-27.5, 34.2) * mm});
            skLineSegment(sketch, "E395", {"start": v(-26, 38.2) * mm, "end": v(-26, 34.9) * mm});
            skLineSegment(sketch, "E396", {"start": v(-27.5, 34.2) * mm, "end": v(-27.5, 34.45) * mm});
            skLineSegment(sketch, "E397", {"start": v(-27.5, 30.75) * mm, "end": v(-27.5, 31) * mm});
            skLineSegment(sketch, "E398", {"start": v(-27.5, 31) * mm, "end": v(-26.7, 31) * mm});
            skArc(sketch, "E399", {"start": v(3.16, 22.6) * mm, "mid": v(3.2, 22.7) * mm, "end": v(3.23, 22.8) * mm});
            skLineSegment(sketch, "E400", {"start": v(3.23, 22.8) * mm, "end": v(3.79, 25.69) * mm});
            skArc(sketch, "E401", {"start": v(3.79, 25.69) * mm, "mid": v(3.25, 26.57) * mm, "end": v(2.32, 26.12) * mm});
            skLineSegment(sketch, "E402", {"start": v(2.32, 26.12) * mm, "end": v(0.93, 22.67) * mm});
            skArc(sketch, "E403", {"start": v(0.93, 22.67) * mm, "mid": v(0.88, 22.55) * mm, "end": v(0.82, 22.43) * mm});
            skLineSegment(sketch, "E404", {"start": v(0.82, 22.43) * mm, "end": v(-1.5, 17.45) * mm});
            skLineSegment(sketch, "E405", {"start": v(-1.5, 17.45) * mm, "end": v(-1.5, 17.2) * mm});
            skArc(sketch, "E406", {"start": v(-1, 14.9) * mm, "mid": v(-1.2, 14.4) * mm, "end": v(-1.7, 14.2) * mm});
            skArc(sketch, "E407", {"start": v(-2.5, 14.45) * mm, "mid": v(-2.83, 14.69) * mm, "end": v(-2.95, 14.3) * mm});
            skLineSegment(sketch, "E408", {"start": v(-2.95, 14.3) * mm, "end": v(-2.68, 13.92) * mm});
            skArc(sketch, "E409", {"start": v(-2.68, 13.92) * mm, "mid": v(-2.55, 13.64) * mm, "end": v(-2.5, 13.34) * mm});
            skLineSegment(sketch, "E410", {"start": v(-2.5, 13.34) * mm, "end": v(-2.5, 11.86) * mm});
            skArc(sketch, "E411", {"start": v(-2.5, 11.86) * mm, "mid": v(-2.55, 11.56) * mm, "end": v(-2.68, 11.28) * mm});
            skLineSegment(sketch, "E412", {"start": v(-2.68, 11.28) * mm, "end": v(-2.95, 10.9) * mm});
            skArc(sketch, "E413", {"start": v(-2.95, 10.9) * mm, "mid": v(-2.83, 10.51) * mm, "end": v(-2.5, 10.75) * mm});
            skArc(sketch, "E414", {"start": v(-1.7, 11) * mm, "mid": v(-1.45, 10.95) * mm, "end": v(-1.24, 10.83) * mm});
            skArc(sketch, "E415", {"start": v(-1.24, 10.83) * mm, "mid": v(-0.96, 10.7) * mm, "end": v(-0.67, 10.76) * mm});
            skArc(sketch, "E416", {"start": v(-0.67, 10.76) * mm, "mid": v(0.19, 11.59) * mm, "end": v(0.5, 12.73) * mm});
            skLineSegment(sketch, "E417", {"start": v(0.5, 12.73) * mm, "end": v(0.5, 15.46) * mm});
            skArc(sketch, "E418", {"start": v(0.5, 15.46) * mm, "mid": v(0.6, 16.48) * mm, "end": v(0.92, 17.45) * mm});
            skLineSegment(sketch, "E419", {"start": v(0.92, 17.45) * mm, "end": v(3.16, 22.6) * mm});
            skArc(sketch, "E420", {"start": v(-20.9, 39.32) * mm, "mid": v(-21.2, 39.76) * mm, "end": v(-21.72, 39.69) * mm});
            skArc(sketch, "E421", {"start": v(-21.72, 39.69) * mm, "mid": v(-21.72, 39.7) * mm, "end": v(-21.72, 39.7) * mm});
            skArc(sketch, "E422", {"start": v(-21.72, 39.7) * mm, "mid": v(-23.77, 38.7) * mm, "end": v(-26, 38.2) * mm});
            skArc(sketch, "E423", {"start": v(-26, 34.9) * mm, "mid": v(-26.2, 34.4) * mm, "end": v(-26.7, 34.2) * mm});
            skArc(sketch, "E424", {"start": v(-27.5, 34.45) * mm, "mid": v(-27.83, 34.69) * mm, "end": v(-27.95, 34.3) * mm});
            skLineSegment(sketch, "E425", {"start": v(-27.95, 34.3) * mm, "end": v(-27.68, 33.92) * mm});
            skArc(sketch, "E426", {"start": v(-27.68, 33.92) * mm, "mid": v(-27.55, 33.64) * mm, "end": v(-27.5, 33.34) * mm});
            skLineSegment(sketch, "E427", {"start": v(-27.5, 33.34) * mm, "end": v(-27.5, 31.86) * mm});
            skArc(sketch, "E428", {"start": v(-27.5, 31.86) * mm, "mid": v(-27.55, 31.56) * mm, "end": v(-27.68, 31.28) * mm});
            skLineSegment(sketch, "E429", {"start": v(-27.68, 31.28) * mm, "end": v(-27.95, 30.9) * mm});
            skArc(sketch, "E430", {"start": v(-27.95, 30.9) * mm, "mid": v(-27.83, 30.51) * mm, "end": v(-27.5, 30.75) * mm});
            skArc(sketch, "E431", {"start": v(-26.7, 31) * mm, "mid": v(-26.2, 30.8) * mm, "end": v(-26, 30.3) * mm});
            skArc(sketch, "E432", {"start": v(-26, 30.3) * mm, "mid": v(-25.98, 30.2) * mm, "end": v(-25.94, 30.12) * mm});
            skLineSegment(sketch, "E433", {"start": v(-25.94, 30.12) * mm, "end": v(-24.84, 28.62) * mm});
            skArc(sketch, "E434", {"start": v(-24.84, 28.62) * mm, "mid": v(-24.61, 28.5) * mm, "end": v(-24.37, 28.6) * mm});
            skArc(sketch, "E435", {"start": v(-24.37, 28.6) * mm, "mid": v(-22.6, 31.36) * mm, "end": v(-21.72, 34.52) * mm});
            skArc(sketch, "E436", {"start": v(-21.72, 34.52) * mm, "mid": v(-21.66, 34.67) * mm, "end": v(-21.53, 34.77) * mm});
            skLineSegment(sketch, "E437", {"start": v(-21.53, 34.77) * mm, "end": v(-21.08, 34.93) * mm});
            skArc(sketch, "E438", {"start": v(-21.08, 34.93) * mm, "mid": v(-20.93, 34.92) * mm, "end": v(-20.83, 34.8) * mm});
            skArc(sketch, "E439", {"start": v(-20.83, 34.8) * mm, "mid": v(-20.34, 33.58) * mm, "end": v(-19.75, 32.4) * mm});
            skArc(sketch, "E440", {"start": v(-19.75, 32.4) * mm, "mid": v(-19.2, 32.25) * mm, "end": v(-19.05, 32.79) * mm});
            skArc(sketch, "E441", {"start": v(-19.05, 32.79) * mm, "mid": v(-20.35, 35.95) * mm, "end": v(-20.9, 39.32) * mm});
            skLineSegment(sketch, "E442", {"start": v(-24.9, 35.57) * mm, "end": v(-24.9, 36.91) * mm});
            skArc(sketch, "E443", {"start": v(-24.9, 36.91) * mm, "mid": v(-24.87, 37.03) * mm, "end": v(-24.78, 37.1) * mm});
            skArc(sketch, "E444", {"start": v(-24.78, 37.1) * mm, "mid": v(-23.31, 37.84) * mm, "end": v(-22, 38.8) * mm});
            skArc(sketch, "E445", {"start": v(-22, 38.8) * mm, "mid": v(-21.78, 38.84) * mm, "end": v(-21.66, 38.68) * mm});
            skArc(sketch, "E446", {"start": v(-21.66, 38.68) * mm, "mid": v(-21.48, 37.3) * mm, "end": v(-21.18, 35.93) * mm});
            skArc(sketch, "E447", {"start": v(-21.18, 35.93) * mm, "mid": v(-21.2, 35.72) * mm, "end": v(-21.36, 35.57) * mm});
            skLineSegment(sketch, "E448", {"start": v(-21.36, 35.57) * mm, "end": v(-21.76, 35.43) * mm});
            skArc(sketch, "E449", {"start": v(-21.76, 35.43) * mm, "mid": v(-22.2, 35.11) * mm, "end": v(-22.42, 34.6) * mm});
            skArc(sketch, "E450", {"start": v(-22.42, 34.6) * mm, "mid": v(-23.06, 32.07) * mm, "end": v(-24.33, 29.77) * mm});
            skArc(sketch, "E451", {"start": v(-24.33, 29.77) * mm, "mid": v(-24.57, 29.65) * mm, "end": v(-24.81, 29.77) * mm});
            skLineSegment(sketch, "E452", {"start": v(-24.81, 29.77) * mm, "end": v(-25.14, 30.22) * mm});
            skArc(sketch, "E453", {"start": v(-25.14, 30.22) * mm, "mid": v(-25.18, 30.3) * mm, "end": v(-25.2, 30.4) * mm});
            skLineSegment(sketch, "E454", {"start": v(-25.2, 30.4) * mm, "end": v(-25.2, 30.98) * mm});
            skArc(sketch, "E455", {"start": v(-25.2, 30.98) * mm, "mid": v(-25.22, 31.09) * mm, "end": v(-25.28, 31.18) * mm});
            skArc(sketch, "E456", {"start": v(-25.28, 31.18) * mm, "mid": v(-25.89, 32.58) * mm, "end": v(-25.57, 34.07) * mm});
            skArc(sketch, "E457", {"start": v(-25.57, 34.07) * mm, "mid": v(-25.23, 34.35) * mm, "end": v(-24.8, 34.32) * mm});
            skLineSegment(sketch, "E458", {"start": v(-24.8, 34.32) * mm, "end": v(-24.37, 34.12) * mm});
            skArc(sketch, "E459", {"start": v(-24.37, 34.12) * mm, "mid": v(-23.84, 34.31) * mm, "end": v(-24.03, 34.84) * mm});
            skLineSegment(sketch, "E460", {"start": v(-24.03, 34.84) * mm, "end": v(-24.61, 35.12) * mm});
            skArc(sketch, "E461", {"start": v(-24.61, 35.12) * mm, "mid": v(-24.82, 35.3) * mm, "end": v(-24.9, 35.57) * mm});
            skSolve(sketch);
        }
        {
            var Q0;
            {var subQ3=sQuery(id+"F0.wireOp",EDGE,"E269");Q0=makeQuery(id+"F0.imprint","IMPRINT",FACE,{"disambiguationData":[TD([[makeQuery(id+"F0.imprint","IMPRINT",EDGE,{"derivedFrom":subQ3}),-1.0]])]});}
            var Q1;
            {var subQ2=sQuery(id+"F0.wireOp",EDGE,"E359");Q1=makeQuery(id+"F0.imprint","IMPRINT",FACE,{"disambiguationData":[TD([[makeQuery(id+"F0.imprint","IMPRINT",EDGE,{"derivedFrom":subQ2}),-1.0]])]});}
            extrude(context, id + "F1", {"entities" : qUnion([Q0, Q1]), "depth" : 250 * mm, "offsetDistance" : 25 * mm});
        }
        {
            var Q0;
            Q0=makeQuery(id+"F0.imprint","IMPRINT",FACE,{"disambiguationData":[TD([[makeQuery(id+"F0.imprint","IMPRINT",EDGE,{"derivedFrom":sQuery(id+"F0.wireOp",EDGE,"E0")}),1.0]])]});
            extrude(context, id + "F2", {"entities" : qUnion([Q0]), "depth" : 250 * mm, "offsetDistance" : 25 * mm});
        }
        {
            var Q0;
            Q0=makeQuery(id+"F2.opExtrude","SWEPT_FACE",FACE,{"disambiguationData":[OSD([sQuery(id+"F0.wireOp",EDGE,"E355")])]});
            var sketch = newSketch(context, id + "F3", { "sketchPlane" : qUnion([Q0])});
            skLineSegment(sketch, "E462.left", {"start": v(5, -58.1) * mm, "end": v(5, -158.1) * mm});
            skLineSegment(sketch, "E462.right", {"start": v(26, -58.1) * mm, "end": v(26, -158.1) * mm});
            skArc(sketch, "E463", {"start": v(26, -58.1) * mm, "mid": v(15.5, -47.6) * mm, "end": v(5, -58.1) * mm});
            skArc(sketch, "E464", {"start": v(5, -158.1) * mm, "mid": v(15.5, -168.6) * mm, "end": v(26, -158.1) * mm});
            skSolve(sketch);
        }
        {
            var Q0;
            Q0=makeQuery(id+"F3.imprint","IMPRINT",FACE,{"disambiguationData":[TD([[makeQuery(id+"F3.imprint","IMPRINT",EDGE,{"derivedFrom":sQuery(id+"F3.wireOp",EDGE,"E462.left")}),1.0]])]});
            extrude(context, id + "F4", {"entities" : qUnion([Q0]), "operationType" : NewBodyOperationType.REMOVE, "endBound" : BoundingType.UP_TO_NEXT, "oppositeDirection" : true, "depth" : 25 * mm, "offsetDistance" : 25 * mm});
        }
    });
